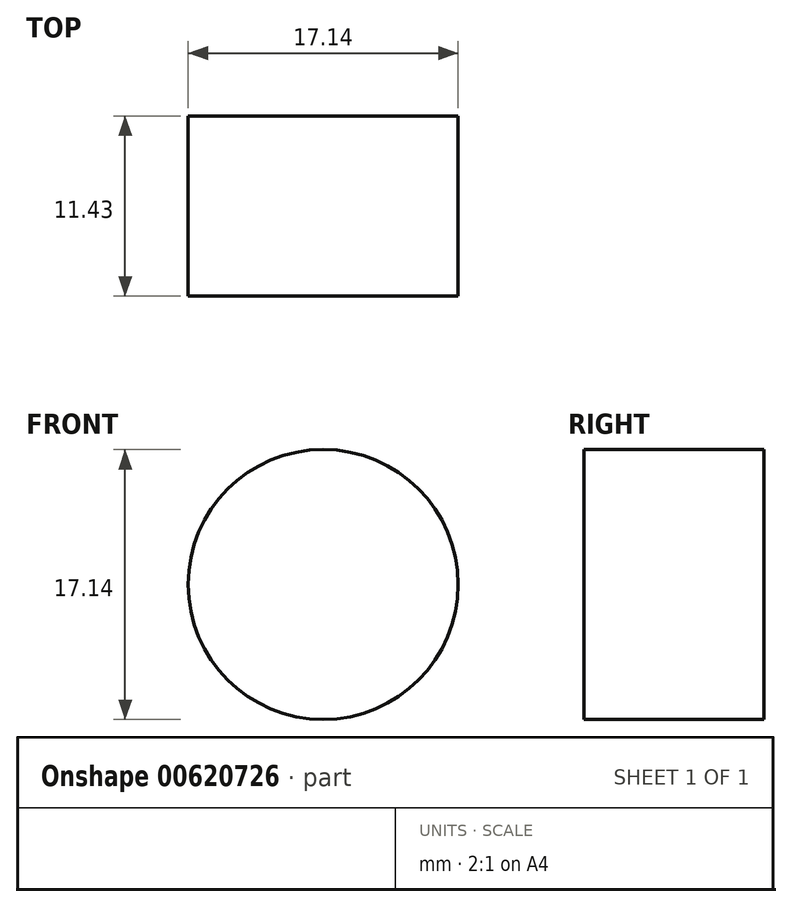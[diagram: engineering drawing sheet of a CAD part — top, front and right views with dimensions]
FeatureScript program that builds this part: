
annotation { "Feature Type Name" : "Feature", "Feature Type Description" : "" }
export const myFeature = defineFeature(function(context is Context, id is Id, definition is map)
    precondition{}
    {
        {
            var Q0;
            Q0=qCreatedBy(makeId("Front.planeOp"),FACE);
            var sketch = newSketch(context, id + "F0", { "sketchPlane" : qUnion([Q0])});
            skCircle(sketch, "E0", {"center": v(0, 0) * mm, "radius": 8.57 * mm});
            skSolve(sketch);
        }
        {
            var Q0;
            Q0=qSketchRegion(id+"F0",true);
            extrude(context, id + "F1", {"entities" : qUnion([Q0]), "depth" : 11.43 * mm, "offsetDistance" : 25.4 * mm});
        }
    });
